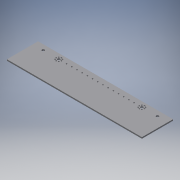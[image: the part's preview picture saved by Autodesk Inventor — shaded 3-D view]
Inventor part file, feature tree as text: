
AUTODESK INVENTOR PART (.ipt)
format: ipt  version: 2016 (Build 200138000, 138)  size: 157,696 bytes
history: native  units: mm
features: reference x46, sketch x3, hole x2, extrude x1
ambient origin geometry x8: Origin, YZ Plane, XZ Plane, XY Plane, X Axis, Y Axis, Z Axis, Center Point
bodies: Body1 (feature_tree)
feature tree (52):
  extrude  "Extrusion2"  Depth=96.0mm
  sketch  "Sketch2"  dims[d4=4.0mm d5=0.0mm]
  sketch  "Sketch3"  dims[d6=8.0mm d7=6.0mm d8=4.0mm d9=2.0mm d10=90.0deg d11=8.0mm d12=20.594885mm d13=3.7mm d14=6.0mm d15=4.0mm d16=2.0mm d17=90.0deg d18=8.0mm d19=20.594885mm]
  hole  "Hole1"  [1 undecoded]
  hole  "Hole2"  [1 undecoded]
  sketch  "Sketch1"  dims[d0=416.0mm d1=96.0mm]
  reference  "Reference1"
  reference  "Reference2"
  reference  "Reference3"
  reference  "Reference4"
  reference  "Reference5"
  reference  "Reference6"
  reference  "Reference7"
  reference  "Reference8"
  reference  "Reference9"
  reference  "Reference10"
  reference  "Reference11"
  reference  "Reference12"
  reference  "Reference13"
  reference  "Reference14"
  reference  "Reference15"
  reference  "Reference16"
  reference  "Reference17"
  reference  "Reference18"
  reference  "Reference19"
  reference  "Reference20"
  reference  "Reference21"
  reference  "Reference22"
  reference  "Reference23"
  reference  "Reference24"
  reference  "Reference25"
  reference  "Reference26"
  reference  "Reference27"
  reference  "Reference28"
  reference  "Reference29"
  reference  "Reference30"
  reference  "Reference31"
  reference  "Reference32"
  reference  "Reference33"
  reference  "Reference34"
  reference  "Reference35"
  reference  "Reference40"
  reference  "Reference41"
  reference  "Reference42"
  reference  "Reference43"
  reference  "Reference44"
  reference  "Reference45"
  reference  "Reference46"
  reference  "Reference47"
  reference  "Reference48"
  reference  "Reference49"
  reference  "Reference50"
note: 2 required parameter values undecoded (feature->parameter linkage not recoverable at this tier; creation-order binding heuristic only, values carry confidence <= 0.55)
